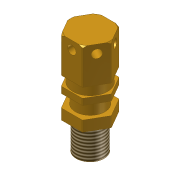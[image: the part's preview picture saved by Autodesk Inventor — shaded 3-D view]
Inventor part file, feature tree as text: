
AUTODESK INVENTOR PART (.ipt)
format: ipt  version: unknown  size: 291,328 bytes
history: native  units: mm (DEFAULTED — no unit token found)
features: sketch x9, projected_geometry x9, extrude x8, pattern_circular x1, thread x1, fillet x1, revolve x1
ambient origin geometry x8: Origin, YZ Plane, XZ Plane, XY Plane, X Axis, Y Axis, Z Axis, Center Point
feature tree (30):
  extrude  "Extrusion1"  Depth=17.0mm TaperAngle=0.0deg
  extrude  "Extrusion2"  Depth=4.5mm TaperAngle=0.0deg
  extrude  "Extrusion3"  Depth=14.0mm
  extrude  "Extrusion4"  Depth=5.0mm TaperAngle=0.0deg
  extrude  "Extrusion5"  Depth=14.5mm TaperAngle=0.0deg
  extrude  "Extrusion6"  Depth=47.5mm TaperAngle=0.0deg
  extrude  "Extrusion7"  Depth=4.0mm
  extrude  "Extrusion8"  Depth=30.0mm TaperAngle=360.0deg
  pattern_circular  "Circular Pattern1"  Angle=45.0deg  [1 undecoded]
  thread  "Thread1"  [1 undecoded]
  fillet  "Fillet1"  [1 undecoded]
  revolve  "Revolution2"  [1 undecoded]
  sketch  "Sketch1"  dims[d0=17.5mm d1=17.0mm d2=0.0mm]
  sketch  "Sketch2"  dims[d3=16.5mm d4=4.5mm d5=0.0mm]
  projected_geometry  "Projected Loop1"
  sketch  "Sketch3"  dims[d6=3.0mm d7=0.0mm d8=14.0mm]
  projected_geometry  "Projected Loop2"
  sketch  "Sketch4"  dims[d9=6.0mm d10=0.0mm d11=5.0mm d12=0.0mm]
  projected_geometry  "Projected Loop3"
  sketch  "Sketch5"  dims[d13=13.25mm d14=14.5mm d15=0.0mm]
  projected_geometry  "Projected Loop4"
  sketch  "Sketch6"  dims[d16=5.0mm d17=47.5mm d18=0.0mm]
  projected_geometry  "Projected Loop5"
  sketch  "Sketch7"  dims[d19=4.0mm d20=4.0mm]
  projected_geometry  "Projected Loop6"
  sketch  "Sketch8"  dims[d21=40.25mm d22=0.0mm d23=30.0mm d25=360.0deg]
  projected_geometry  "Projected Loop7"
  sketch  "Sketch10"  dims[d26=10.0mm d27=0.0mm d28=0.5mm d32=45.0deg d33=1.0mm d34=90.0deg]
  projected_geometry  "Projected Loop8"
  projected_geometry  "Projected Loop9"
note: 4 required parameter values undecoded (feature->parameter linkage not recoverable at this tier; creation-order binding heuristic only, values carry confidence <= 0.55)
